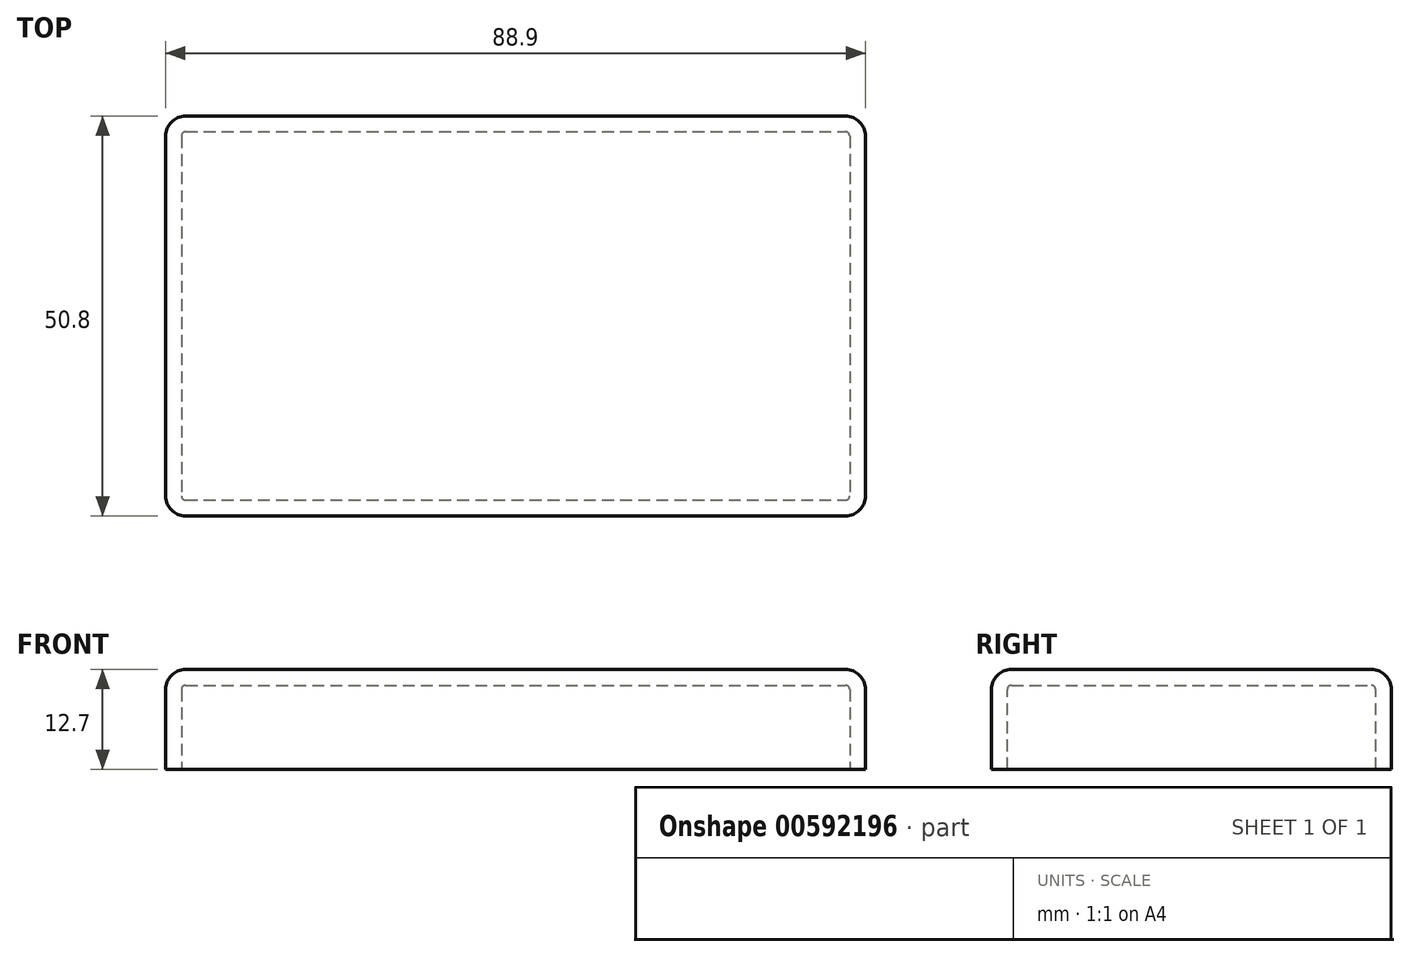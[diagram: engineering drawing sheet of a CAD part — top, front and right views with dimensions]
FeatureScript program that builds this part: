
annotation { "Feature Type Name" : "Feature", "Feature Type Description" : "" }
export const myFeature = defineFeature(function(context is Context, id is Id, definition is map)
    precondition{}
    {
        {
            var Q0;
            Q0=qCreatedBy(makeId("Top.planeOp"),FACE);
            var sketch = newSketch(context, id + "F0", { "sketchPlane" : qUnion([Q0])});
            skLineSegment(sketch, "E0.bottom", {"start": v(-44.45, 25.4) * mm, "end": v(44.45, 25.4) * mm});
            skLineSegment(sketch, "E0.top", {"start": v(-44.45, -25.4) * mm, "end": v(44.45, -25.4) * mm});
            skLineSegment(sketch, "E0.left", {"start": v(-44.45, 25.4) * mm, "end": v(-44.45, -25.4) * mm});
            skLineSegment(sketch, "E0.right", {"start": v(44.45, 25.4) * mm, "end": v(44.45, -25.4) * mm});
            skPoint(sketch, "E0.middle", {"position": v(0, 0) * mm});
            skSolve(sketch);
        }
        {
            var Q0;
            Q0=makeQuery(id+"F0.imprint","IMPRINT",FACE,{"disambiguationData":[TD([[makeQuery(id+"F0.imprint","IMPRINT",EDGE,{"derivedFrom":sQuery(id+"F0.wireOp",EDGE,"E0.bottom")}),-1.0]])]});
            extrude(context, id + "F1", {"entities" : qUnion([Q0]), "depth" : 12.7 * mm, "offsetDistance" : 25.4 * mm});
        }
        {
            var Q0;
            Q0=makeQuery(id+"F1.opExtrude","CAP_EDGE",EDGE,{"disambiguationData":[OSD([sQuery(id+"F0.wireOp",EDGE,"E0.top")])],"isStart":false});
            var Q1;
            Q1=makeQuery(id+"F1.opExtrude","CAP_EDGE",EDGE,{"disambiguationData":[OSD([sQuery(id+"F0.wireOp",EDGE,"E0.bottom")])],"isStart":false});
            var Q2;
            Q2=makeQuery(id+"F1.opExtrude","CAP_EDGE",EDGE,{"disambiguationData":[OSD([sQuery(id+"F0.wireOp",EDGE,"E0.right")])],"isStart":false});
            var Q3;
            Q3=makeQuery(id+"F1.opExtrude","CAP_EDGE",EDGE,{"disambiguationData":[OSD([sQuery(id+"F0.wireOp",EDGE,"E0.left")])],"isStart":false});
            var Q4;
            Q4=makeQuery(id+"F1.opExtrude","SWEPT_EDGE",EDGE,{"disambiguationData":[OSD([sQuery(id+"F0.wireOp",EDGE,"E0.bottom"),sQuery(id+"F0.wireOp",EDGE,"E0.left")])]});
            var Q5;
            Q5=makeQuery(id+"F1.opExtrude","SWEPT_EDGE",EDGE,{"disambiguationData":[OSD([sQuery(id+"F0.wireOp",EDGE,"E0.top"),sQuery(id+"F0.wireOp",EDGE,"E0.left")])]});
            var Q6;
            Q6=makeQuery(id+"F1.opExtrude","SWEPT_EDGE",EDGE,{"disambiguationData":[OSD([sQuery(id+"F0.wireOp",EDGE,"E0.top"),sQuery(id+"F0.wireOp",EDGE,"E0.right")])]});
            var Q7;
            Q7=makeQuery(id+"F1.opExtrude","SWEPT_EDGE",EDGE,{"disambiguationData":[OSD([sQuery(id+"F0.wireOp",EDGE,"E0.bottom"),sQuery(id+"F0.wireOp",EDGE,"E0.right")])]});
            fillet(context, id + "F2", {"entities" : qUnion([Q0, Q1, Q2, Q3, Q4, Q5, Q6, Q7]), "radius" : 2.54 * mm, "tangentPropagation" : true, "allowEdgeOverflow" : false});
        }
        {
            var Q0;
            Q0=makeQuery(id+"F1.opExtrude","CAP_FACE",FACE,{"disambiguationData":[OSD([sQuery(id+"F0.wireOp",EDGE,"E0.bottom"),sQuery(id+"F0.wireOp",EDGE,"E0.top"),sQuery(id+"F0.wireOp",EDGE,"E0.left"),sQuery(id+"F0.wireOp",EDGE,"E0.right")])],"isStart":true});
            shell(context, id + "F3", {"entities" : qUnion([Q0]), "thickness" : 2 * mm});
        }
    });
